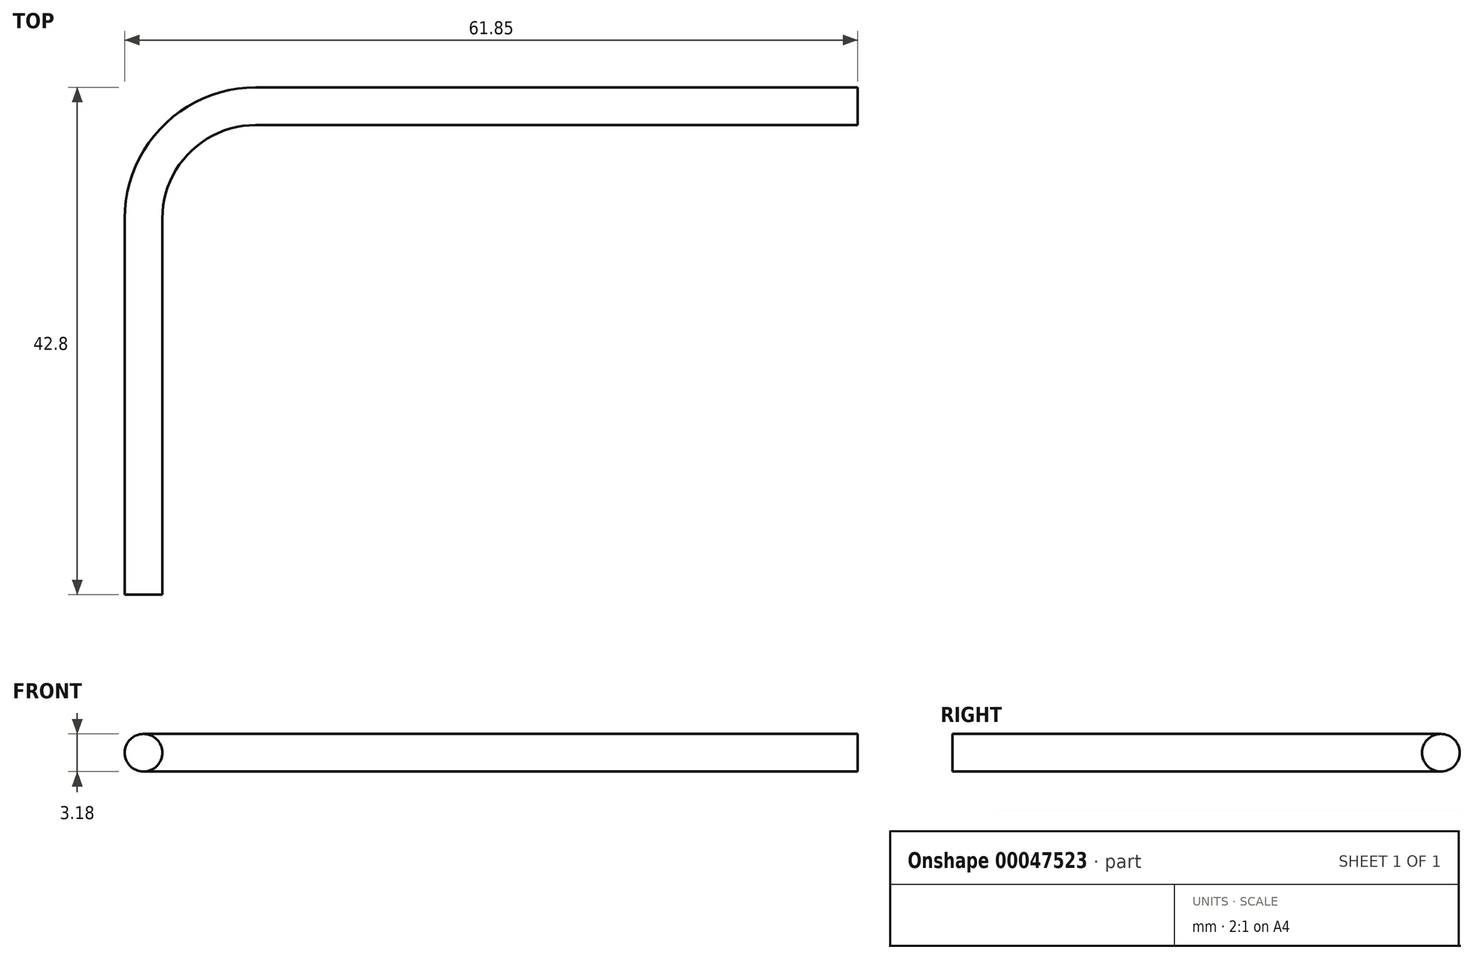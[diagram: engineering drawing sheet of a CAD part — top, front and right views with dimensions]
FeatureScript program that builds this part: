
annotation { "Feature Type Name" : "Feature", "Feature Type Description" : "" }
export const myFeature = defineFeature(function(context is Context, id is Id, definition is map)
    precondition{}
    {
        {
            var Q0;
            Q0=qCreatedBy(makeId("Top.planeOp"),FACE);
            var sketch = newSketch(context, id + "F0", { "sketchPlane" : qUnion([Q0])});
            skArc(sketch, "E0", {"start": v(0, 7.87) * mm, "mid": v(-5.57, 5.57) * mm, "end": v(-7.87, 0) * mm});
            skLineSegment(sketch, "E1", {"start": v(-7.87, 0) * mm, "end": v(-7.87, -31.75) * mm});
            skLineSegment(sketch, "E2", {"start": v(0, 7.87) * mm, "end": v(50.8, 7.87) * mm});
            skPoint(sketch, "E3", {"position": v(-7.87, -31.75) * mm});
            skPoint(sketch, "E4", {"position": v(-7.87, 0) * mm});
            skSolve(sketch);
        }
        {
            var Q0;
            Q0=qCreatedBy(makeId("Front.planeOp"),FACE);
            var Q1;
            Q1=sQuery(id+"F0.wireOp",VERTEX,"E3");
            cPlane(context, id + "F1", {"entities" : qUnion([Q0, Q1]), "cplaneType" : CPlaneType.PLANE_POINT, "offset" : 152.4 * mm, "width" : 152.4 * mm, "height" : 152.4 * mm});
        }
        {
            var Q0;
            Q0=qCreatedBy(id+"F1.planeOp",FACE);
            var sketch = newSketch(context, id + "F2", { "sketchPlane" : qUnion([Q0])});
            skCircle(sketch, "E5", {"center": v(-9.46, 0) * mm, "radius": 1.59 * mm});
            skPoint(sketch, "E6.0.end.orphan", {"position": v(0, 0) * mm});
            skPoint(sketch, "E6.0.start.orphan", {"position": v(-7.87, 0) * mm});
            skLineSegment(sketch, "E7.0", {"start": v(-7.87, 0) * mm, "end": v(0, 0) * mm, "construction": true});
            skLineSegment(sketch, "E8", {"start": v(-7.87, 7.3) * mm, "end": v(-7.87, -8.72) * mm, "construction": true});
            skSolve(sketch);
        }
        {
            var Q0;
            Q0 = qSketchRegion(id + "F2", true);
            var Q1;
            Q1 = qConstructionFilter(qBodyType(qCreatedBy(id + "F0" ,EDGE), BodyType.WIRE), ConstructionObject.NO);
            sweep(context, id + "F3", {"profiles" : qUnion([Q0]), "path" : qUnion([Q1])});
        }
    });
